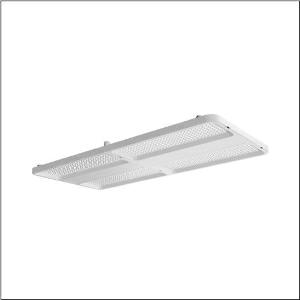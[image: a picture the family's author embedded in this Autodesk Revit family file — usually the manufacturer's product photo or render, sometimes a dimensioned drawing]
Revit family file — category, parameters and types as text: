
# Revit family: highbay_21_maxi_52hn12db4mea
name_source: partatom
category: Lighting Fixtures
units: mm (PartAtom-declared; Revit-internal decimal feet)

## family parameters
Cut with Voids When Loaded = No
Host = Face
Light Source = No
Part Type = Normal
Room Calculation Point = No
Round Connector Dimension = Use Diameter
Shared = No

## types (1)
- --- (1 x LED, 4230 lm, 22.6 W, 4000K)
    Apparent Load = 23 VA
    CIE Flux Codes = 90 98 100 100 100
    Color Rendering = 80
    Color Temperature = 4000K
    Default Elevation = 1800 mm
    Description = high bay luminaire Highbay 21 maxi; direct symmetric wide distribution, light control with lens of PMMA; UGR ≤ 22 (X = 4H | Y = 8H | S = 0.25H | reflection values 70/50/20); luminous flux: 28.000lm; light colour: 840, colour temperature: 4000K, MacAdam ≤ 3 SDCM (initial), colour rendering: CRI > 80; luminous efficacy: 194,4lm/W; rated service life: 75.000h (L80) at AT= ta max; control: DALI 2; luminaire connection: 2x terminal, 5-pole, max. 2.5mm² with through-wiring: 1x feed-in / 1x feed-out (cable entry for two cables, Ø 8.5..13mm); mains connection: 230..240V, AC/DC 0/50..60Hz; connected load: 144W; protection rating (complete): IP66; insulation class (complete): insulation class I (protective earthing); protection symbol: D; impact resistance: IK08; certification: CE, ENEC, VDE, UKCA; luminaire for central battery installations according to EN 60598-2-22, internal wiring halogen-free; luminaire LABS conformity tested according to VDMA 24364:2018-05; Suitable for use in the food industry according to the specifications of IFS-Food, HACCP and/or BRC; housing frame of high-performance plastic PA6, matt traffic white (RAL 9016); cover of PMMA; dimension (LxWxH): 946 x 442 x 72mm; permissible operating ambient temperature: -40..+65°C (reducing of maximum allowable ambient temperature of 5°C with ceiling mounting); packaging unit: 1 piece; (delivery without accessories; please order mounting accessories separately)
    Height = 72 mm  [stored 0.23622 ft]
    Lamp = 1 x LED
    Lamp Light Flux = 4230 lm
    Lamp Power = 22.6 W
    Lamp count = 1
    Length = 946 mm
    Luminous efficacy = 187 lm/W
    Manufacturer = Siteco
    ModVariant = No
    Model = 52HN12DB4MEA
    Mounting Place = Ceiling
    Mounting Type = Pendant
    Number of Poles = 1
    OnlyDefault = Yes
    Power Factor = 1
    Product Name = Highbay 21 maxi
    Product group = high bay luminaire
    ProductGroupID = 902
    Protection Class = Protection class I
    Protection Degree = IP 66
    RLX_Detail_Level = 1
    RLX_Emergency_Light_Flux = 0 lm
    RLX_Emergency_Type = 0
    RLX_Emergency_Type_DB = No
    RlxData = <blob elided: 128441 chars, md5=d78fc002>
    Socket = socket
    Standby Power = 0 W
    System Light Flux = 4230 lm
    System Power = 23 W
    Type Comments = : DC mode (central or group accumulator) initial emergency light level
    Type Image = l_1363244.jpg
    URL = http://relux.com
    VarID = @adj_019283
    Voltage = 0 V
    Weight = 0.00 kg
    Width = 442 mm

note: [stored X ft] marks values corroborated as IEEE doubles in the binary element streams (Revit-internal decimal feet)

## geometry (parser evidence)
native form markers: Blend x4, Sweep x10
no freeform markers — native parametric forms only
